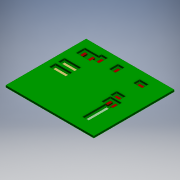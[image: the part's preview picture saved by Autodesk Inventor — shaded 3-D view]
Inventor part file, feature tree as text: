
AUTODESK INVENTOR PART (.ipt)
format: ipt  version: 2016 SP1 (Build 200210100, 210)  size: 579,584 bytes
history: native  units: mm
features: extrude x35, other x28, sketch x2
ambient origin geometry x8: Origin, YZ Plane, XZ Plane, XY Plane, X Axis, Y Axis, Z Axis, Center Point
bodies: Body1 (feature_tree)
feature tree (65):
  other  "Bryła1"
  extrude  "schemat.brd_Kontur"  Depth=1.0mm TaperAngle=0.0deg
  extrude  "C1_2"  Depth=1.0mm
  extrude  "C2_4"  Depth=1.0mm TaperAngle=0.0deg
  extrude  "C3_6"  Depth=1.0mm TaperAngle=0.0deg
  extrude  "C4_8"  Depth=1.0mm TaperAngle=0.0deg
  extrude  "C5_10"  Depth=1.0mm TaperAngle=0.0deg
  extrude  "C6_12"  Depth=1.0mm TaperAngle=0.0deg
  extrude  "C7_14"  Depth=1.0mm TaperAngle=0.0deg
  extrude  "ENKODER1_16"  Depth=1.0mm TaperAngle=0.0deg
  extrude  "ENKODER2_18"  Depth=1.0mm TaperAngle=0.0deg
  extrude  "HV_20"  Depth=1.0mm TaperAngle=0.0deg
  extrude  "IC1_22"  Depth=1.0mm TaperAngle=0.0deg
  extrude  "IC2_24"  Depth=1.0mm TaperAngle=0.0deg
  extrude  "L1_26"  Depth=1.0mm TaperAngle=0.0deg
  extrude  "LED1_28"  Depth=1.0mm TaperAngle=0.0deg
  extrude  "LED2_30"  Depth=1.0mm TaperAngle=0.0deg
  extrude  "LIPOL_32"  Depth=1.0mm TaperAngle=0.0deg
  extrude  "LV_34"  Depth=1.0mm TaperAngle=0.0deg
  extrude  "P-EL-IN_36"  Depth=1.0mm TaperAngle=0.0deg
  extrude  "P-EL-OUT_38"  Depth=1.0mm TaperAngle=0.0deg
  extrude  "P-S-IN_40"  Depth=1.0mm TaperAngle=0.0deg
  extrude  "P-S-OUT_42"  Depth=1.0mm TaperAngle=0.0deg
  extrude  "R1_44"  Depth=1.0mm TaperAngle=0.0deg
  extrude  "R3_46"  Depth=1.0mm TaperAngle=0.0deg
  extrude  "R4_48"  Depth=1.0mm TaperAngle=0.0deg
  extrude  "R5_50"  Depth=1.0mm TaperAngle=0.0deg
  extrude  "R6_52"  Depth=1.0mm TaperAngle=0.0deg
  extrude  "RASPBERRY_54"  Depth=1.0mm TaperAngle=0.0deg
  extrude  "SERWO1_56"  Depth=1.0mm TaperAngle=0.0deg
  extrude  "SERWO2_58"  Depth=1.0mm TaperAngle=0.0deg
  extrude  "SERWO3_60"  Depth=1.0mm TaperAngle=0.0deg
  extrude  "SILNIK1_62"  Depth=1.0mm TaperAngle=0.0deg
  extrude  "SILNIK2_64"  Depth=1.0mm TaperAngle=0.0deg
  extrude  "SPI_66"  Depth=1.0mm TaperAngle=0.0deg
  extrude  "Wyciągnięcie proste35"  Depth=1.0mm TaperAngle=0.0deg
  sketch  "Szkic1"
  other  "C050-030X075, C050-030X075_1"
  other  "C025-030X050, C025-030X050_3"
  other  "C025-030X050, C025-030X050_5"
  other  "C025-030X050, C025-030X050_7"
  other  "C025-030X050, C025-030X050_9"
  other  "E2_5-5, E2_5-5_11"
  other  "E2_5-5, E2_5-5_13"
  other  "1X04, 1X04_15"
  other  "1X04, 1X04_17"
  other  "1X06, 1X06_19"
  other  "DIL28-3, MEGA8-P_21"
  other  "DIL16, L293D_23"
  other  "1X02, 1X02_27"
  other  "1X02, 1X02_29"
  other  "1X02, 1X02_31"
  other  "1X06, 1X06_33"
  other  "1X02, 1X02_35"
  other  "1X02, 1X02_37"
  other  "1X02, 1X02_39"
  other  "1X02, 1X02_41"
  other  "1X02, 1X02_53"
  other  "1X03, 1X03_55"
  other  "1X03, 1X03_57"
  other  "1X03, 1X03_59"
  other  "1X02, 1X02_61"
  other  "1X02, 1X02_63"
  other  "1X07, 1X07_65"
  sketch  "Szkic35"
